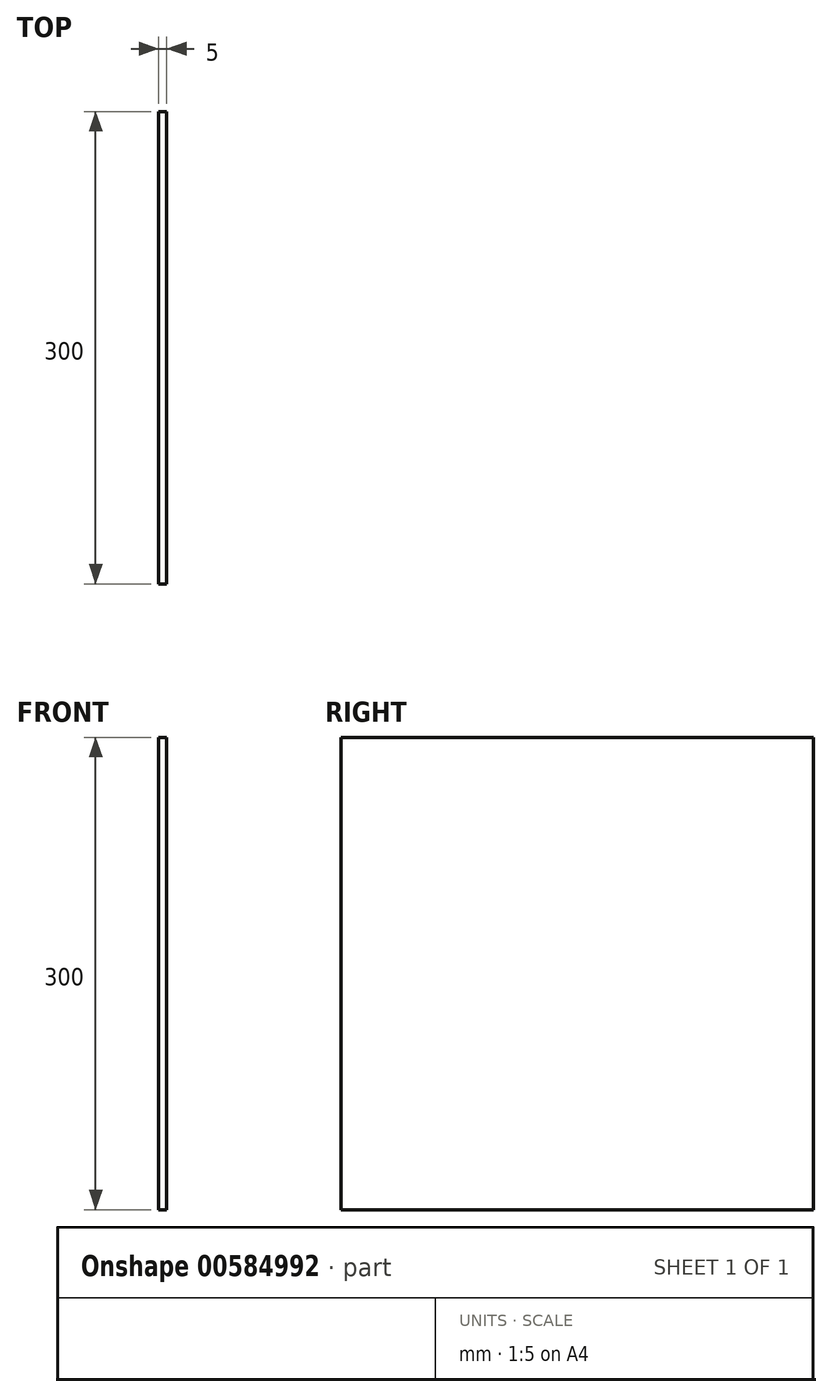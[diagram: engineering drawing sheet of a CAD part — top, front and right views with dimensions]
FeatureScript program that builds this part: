
annotation { "Feature Type Name" : "Feature", "Feature Type Description" : "" }
export const myFeature = defineFeature(function(context is Context, id is Id, definition is map)
    precondition{}
    {
        {
            var Q0;
            Q0=qCreatedBy(makeId("Right.planeOp"),FACE);
            var sketch = newSketch(context, id + "F0", { "sketchPlane" : qUnion([Q0])});
            skLineSegment(sketch, "E0.bottom", {"start": v(-150, 150) * mm, "end": v(150, 150) * mm});
            skLineSegment(sketch, "E0.top", {"start": v(-150, -150) * mm, "end": v(150, -150) * mm});
            skLineSegment(sketch, "E0.left", {"start": v(-150, 150) * mm, "end": v(-150, -150) * mm});
            skLineSegment(sketch, "E0.right", {"start": v(150, 150) * mm, "end": v(150, -150) * mm});
            skPoint(sketch, "E0.middle", {"position": v(0, 0) * mm});
            skSolve(sketch);
        }
        {
            var Q0;
            Q0 = qSketchRegion(id + "F0", true);
            extrude(context, id + "F1", {"entities" : qUnion([Q0]), "depth" : 5 * mm, "offsetDistance" : 25 * mm});
        }
    });
